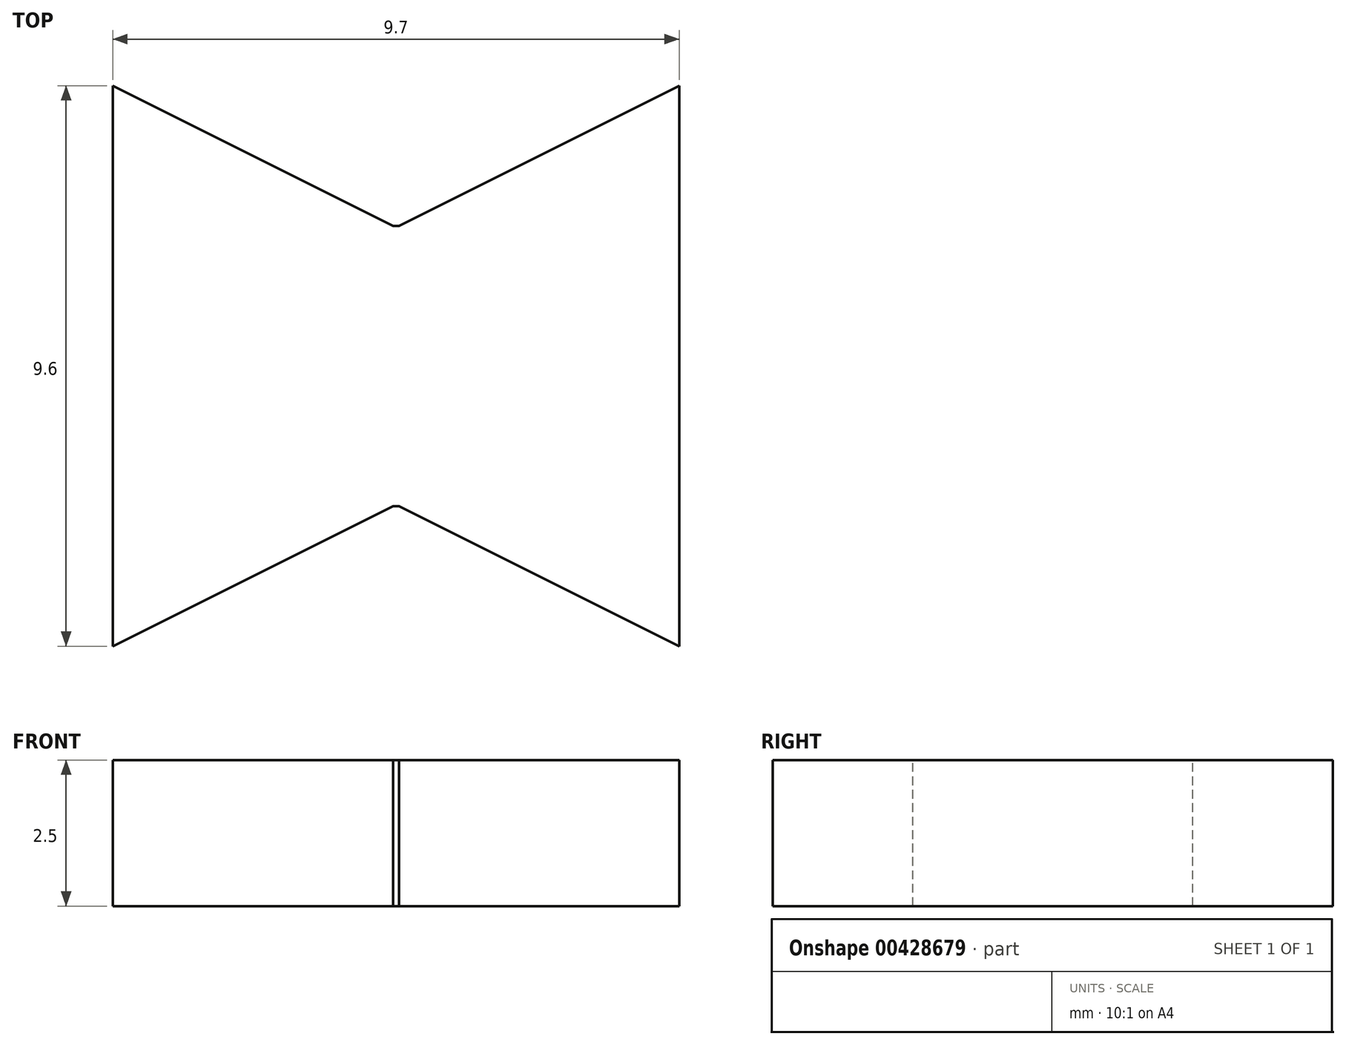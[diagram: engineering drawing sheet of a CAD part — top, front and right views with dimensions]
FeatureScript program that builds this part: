
annotation { "Feature Type Name" : "Feature", "Feature Type Description" : "" }
export const myFeature = defineFeature(function(context is Context, id is Id, definition is map)
    precondition{}
    {
        {
            var Q0;
            Q0=qCreatedBy(makeId("Top.planeOp"),FACE);
            var sketch = newSketch(context, id + "F0", { "sketchPlane" : qUnion([Q0])});
            skLineSegment(sketch, "E0", {"start": v(0.05, 2.4) * mm, "end": v(-0.05, 2.4) * mm});
            skLineSegment(sketch, "E1", {"start": v(-0.05, 2.4) * mm, "end": v(-4.85, 4.8) * mm});
            skLineSegment(sketch, "E2", {"start": v(-4.85, 4.8) * mm, "end": v(-4.85, -4.8) * mm});
            skLineSegment(sketch, "E3", {"start": v(-4.85, -4.8) * mm, "end": v(-0.05, -2.4) * mm});
            skLineSegment(sketch, "E4", {"start": v(-0.05, -2.4) * mm, "end": v(0.05, -2.4) * mm});
            skLineSegment(sketch, "E5", {"start": v(0.05, -2.4) * mm, "end": v(4.85, -4.8) * mm});
            skLineSegment(sketch, "E6", {"start": v(4.85, -4.8) * mm, "end": v(4.85, 4.8) * mm});
            skLineSegment(sketch, "E7", {"start": v(4.85, 4.8) * mm, "end": v(0.05, 2.4) * mm});
            skPoint(sketch, "E8", {"position": v(0, 2.4) * mm});
            skPoint(sketch, "E9", {"position": v(0, -2.4) * mm});
            skPoint(sketch, "E10", {"position": v(-4.85, 0) * mm});
            skPoint(sketch, "E11", {"position": v(4.85, 0) * mm});
            skSolve(sketch);
        }
        {
            var Q0;
            Q0 = qSketchRegion(id + "F0", true);
            extrude(context, id + "F1", {"entities" : qUnion([Q0]), "oppositeDirection" : true, "depth" : 2.5 * mm});
        }
    });
